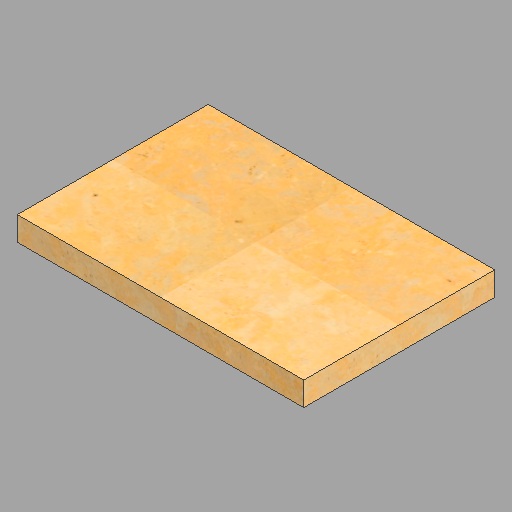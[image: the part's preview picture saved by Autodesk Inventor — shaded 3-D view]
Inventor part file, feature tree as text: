
AUTODESK INVENTOR PART (.ipt)
format: ipt  version: 2023 (Build 270158030, 158C)  size: 249,344 bytes
history: native  units: in
note: dims shown in document units (in); Inventor stores cm internally (conversion verified against a paired STEP export)
features: other x1, extrude x1, sketch x1
ambient origin geometry x8: Origin, YZ Plane, XZ Plane, XY Plane, X Axis, Y Axis, Z Axis, Center Point
bodies: Solid1 (feature_tree)
feature tree (3):
  other  "16x24x2 - 150"
  extrude  "Extrusion1"  Depth=16.0in
  sketch  "Sketch1"  dims[d0=24.0in d1=16.0in d2=2.0in d3=0.0in]
